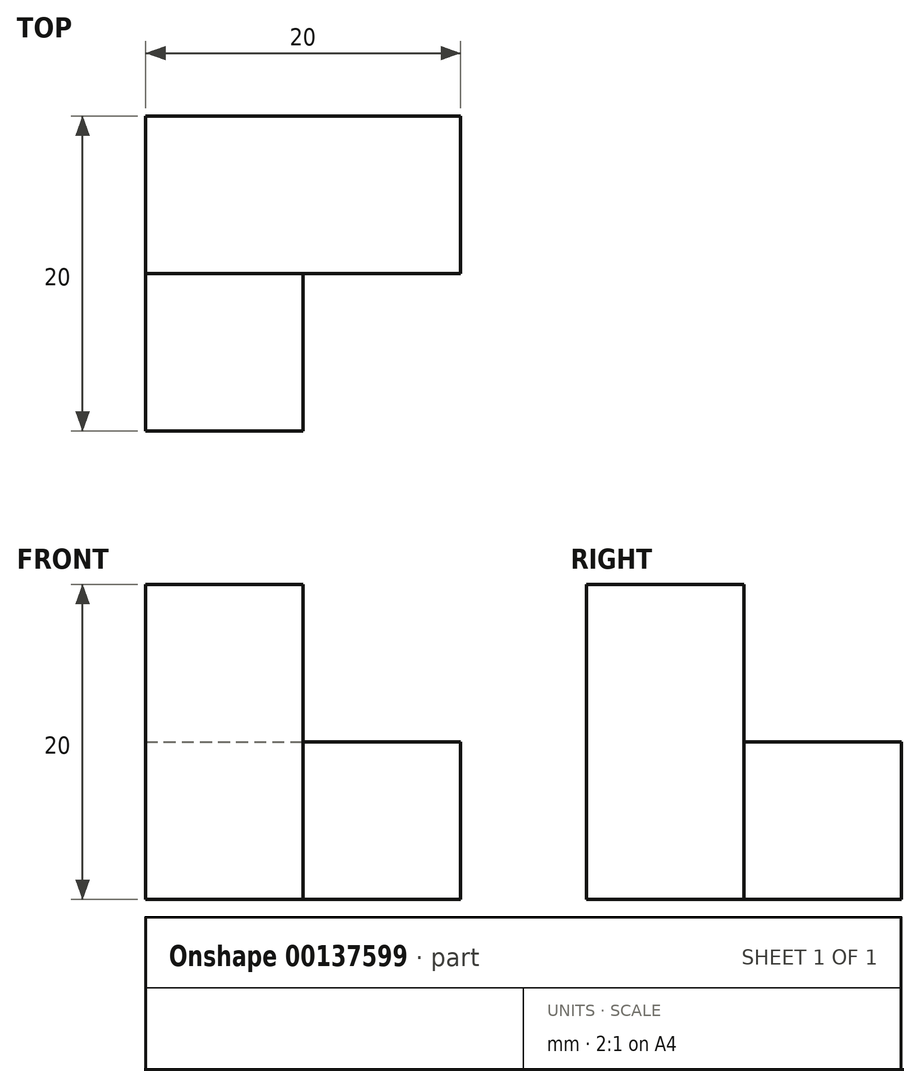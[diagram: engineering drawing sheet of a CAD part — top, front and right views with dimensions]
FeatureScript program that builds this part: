
annotation { "Feature Type Name" : "Feature", "Feature Type Description" : "" }
export const myFeature = defineFeature(function(context is Context, id is Id, definition is map)
    precondition{}
    {
        {
            var Q0;
            Q0=qCreatedBy(makeId("Front.planeOp"),FACE);
            var sketch = newSketch(context, id + "F0", { "sketchPlane" : qUnion([Q0])});
            skLineSegment(sketch, "E0", {"start": v(-20, 20) * mm, "end": v(-20, 0) * mm});
            skLineSegment(sketch, "E1", {"start": v(-20, 0) * mm, "end": v(0, 0) * mm});
            skLineSegment(sketch, "E2", {"start": v(0, 0) * mm, "end": v(0, 10) * mm});
            skLineSegment(sketch, "E3", {"start": v(-20, 20) * mm, "end": v(-10, 20) * mm});
            skLineSegment(sketch, "E4", {"start": v(-10, 20) * mm, "end": v(-10, 10) * mm});
            skLineSegment(sketch, "E5", {"start": v(-10, 10) * mm, "end": v(-10, 0) * mm});
            skLineSegment(sketch, "E6", {"start": v(-10, 10) * mm, "end": v(0, 10) * mm});
            skLineSegment(sketch, "E7", {"start": v(-10, 0) * mm, "end": v(-20, 0) * mm});
            skSolve(sketch);
        }
        {
            var Q0;
            {var subQ1=sQuery(id+"F0.wireOp",EDGE,"E0");Q0=makeQuery(id+"F0.imprint","IMPRINT",FACE,{"disambiguationData":[TD([[makeQuery(id+"F0.imprint","IMPRINT",EDGE,{"derivedFrom":subQ1}),1.0]])]});}
            extrude(context, id + "F1", {"entities" : qUnion([Q0]), "depth" : 10 * mm});
        }
        {
            var Q0;
            Q0=qCreatedBy(makeId("Front.planeOp"),FACE);
            var sketch = newSketch(context, id + "F2", { "sketchPlane" : qUnion([Q0])});
            skLineSegment(sketch, "E8", {"start": v(0, 10) * mm, "end": v(0, 0) * mm});
            skLineSegment(sketch, "E9", {"start": v(0, 0) * mm, "end": v(-20, 0) * mm});
            skLineSegment(sketch, "E10", {"start": v(-20, 0) * mm, "end": v(-20, 10) * mm});
            skLineSegment(sketch, "E11", {"start": v(-20, 10) * mm, "end": v(0, 10) * mm});
            skSolve(sketch);
        }
        {
            var Q0;
            Q0=makeQuery(id+"F2.imprint","IMPRINT",FACE,{"disambiguationData":[TD([[makeQuery(id+"F2.imprint","IMPRINT",EDGE,{"derivedFrom":sQuery(id+"F2.wireOp",EDGE,"E8")}),-1.0]])]});
            extrude(context, id + "F3", {"entities" : qUnion([Q0]), "operationType" : NewBodyOperationType.ADD, "oppositeDirection" : true, "depth" : 10 * mm});
        }
    });
